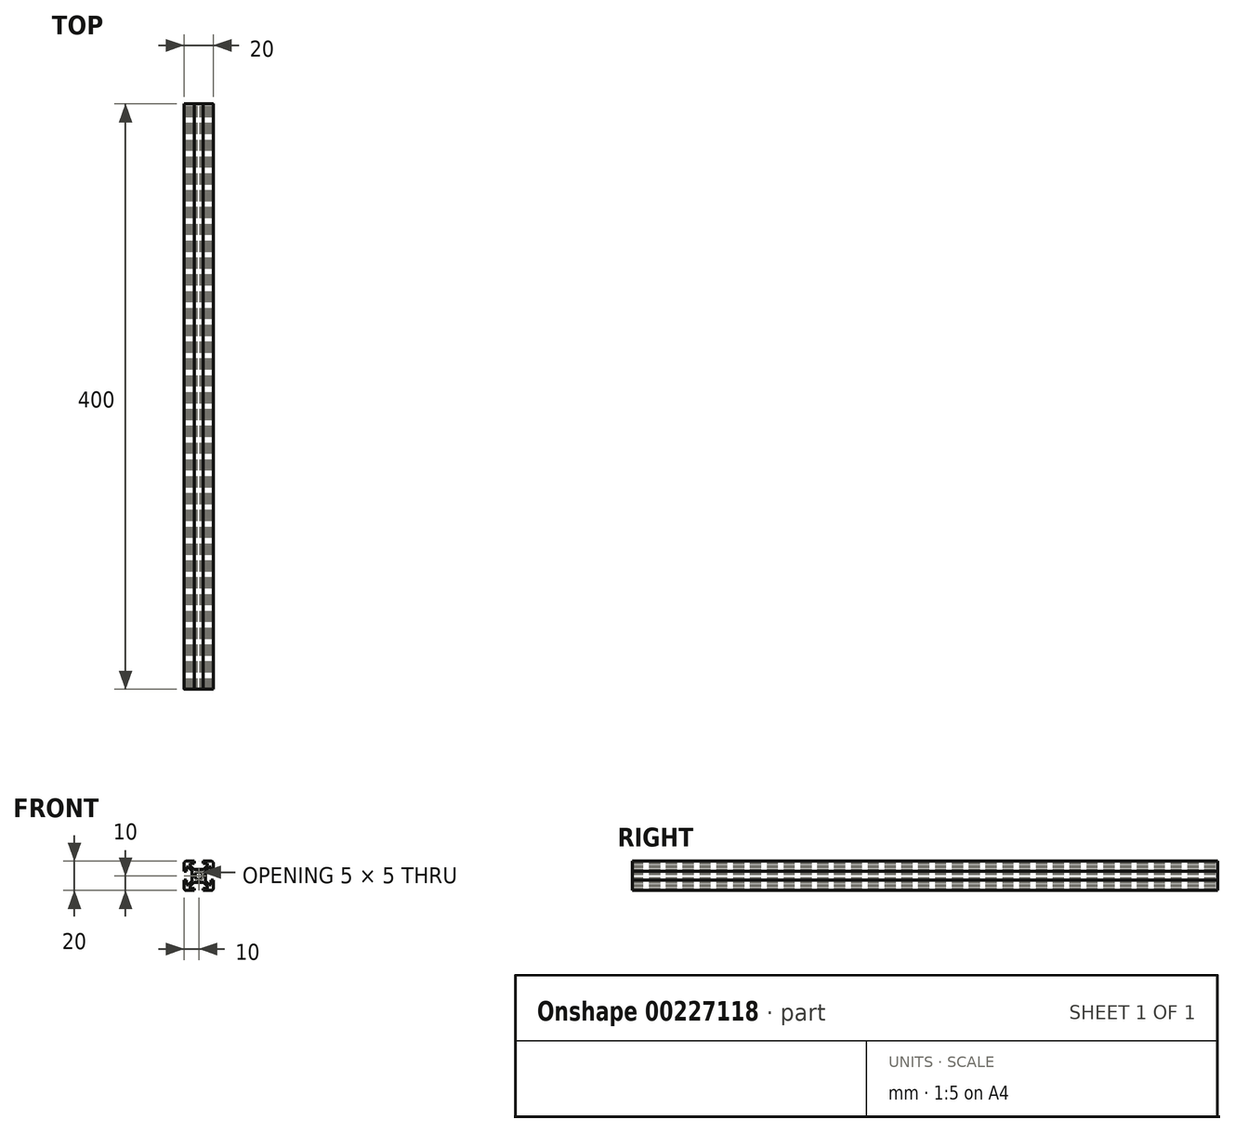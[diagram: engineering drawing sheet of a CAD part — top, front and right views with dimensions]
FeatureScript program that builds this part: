
annotation { "Feature Type Name" : "Feature", "Feature Type Description" : "" }
export const myFeature = defineFeature(function(context is Context, id is Id, definition is map)
    precondition{}
    {
        {
            var Q0;
            Q0=qCreatedBy(makeId("Front.planeOp"),FACE);
            var sketch = newSketch(context, id + "F0", { "sketchPlane" : qUnion([Q0])});
            skLineSegment(sketch, "E0.bottom", {"start": v(8.5, -10) * mm, "end": v(3, -10) * mm});
            skLineSegment(sketch, "E0.top", {"start": v(8.5, 10) * mm, "end": v(3, 10) * mm});
            skLineSegment(sketch, "E0.left", {"start": v(10, -8.5) * mm, "end": v(10, -3) * mm});
            skLineSegment(sketch, "E0.right", {"start": v(-10, -8.5) * mm, "end": v(-10, -3) * mm});
            skPoint(sketch, "E0.middle", {"position": v(0, 0) * mm});
            skLineSegment(sketch, "E1.bottom", {"start": v(6, -8.5) * mm, "end": v(3, -8.5) * mm});
            skLineSegment(sketch, "E1.top", {"start": v(6, 8.5) * mm, "end": v(3, 8.5) * mm});
            skLineSegment(sketch, "E1.left", {"start": v(8.5, -6) * mm, "end": v(8.5, -3) * mm});
            skLineSegment(sketch, "E1.right", {"start": v(-8.5, -6) * mm, "end": v(-8.5, -3) * mm});
            skLineSegment(sketch, "E2.bottom", {"start": v(3.44, -4.5) * mm, "end": v(-3.44, -4.5) * mm});
            skLineSegment(sketch, "E2.top", {"start": v(3.44, 4.5) * mm, "end": v(-3.44, 4.5) * mm});
            skLineSegment(sketch, "E2.left", {"start": v(4.5, -3.44) * mm, "end": v(4.5, 3.44) * mm});
            skLineSegment(sketch, "E2.right", {"start": v(-4.5, -3.44) * mm, "end": v(-4.5, 3.44) * mm});
            skLineSegment(sketch, "E3.bottom", {"start": v(8.5, -6) * mm, "end": v(7.06, -6) * mm});
            skLineSegment(sketch, "E3.top", {"start": v(8.5, 6) * mm, "end": v(7.06, 6) * mm});
            skLineSegment(sketch, "E4.left", {"start": v(6, -8.5) * mm, "end": v(6, -7.06) * mm});
            skLineSegment(sketch, "E4.right", {"start": v(-6, -8.5) * mm, "end": v(-6, -7.06) * mm});
            skPoint(sketch, "E5.orphan", {"position": v(-8.5, 8.5) * mm});
            skPoint(sketch, "E6.orphan", {"position": v(8.5, 8.5) * mm});
            skPoint(sketch, "E7.orphan", {"position": v(8.5, -8.5) * mm});
            skPoint(sketch, "E8.orphan", {"position": v(-8.5, -8.5) * mm});
            skLineSegment(sketch, "E9.trimOffspring", {"start": v(-6, 7.06) * mm, "end": v(-6, 8.5) * mm});
            skLineSegment(sketch, "E10.trimOffspring", {"start": v(-7.06, 6) * mm, "end": v(-8.5, 6) * mm});
            skLineSegment(sketch, "E11.trimOffspring", {"start": v(6, 7.06) * mm, "end": v(6, 8.5) * mm});
            skLineSegment(sketch, "E12.trimOffspring", {"start": v(-7.06, -6) * mm, "end": v(-8.5, -6) * mm});
            skLineSegment(sketch, "E13", {"start": v(-10, 10) * mm, "end": v(0, 0) * mm, "construction": true});
            skLineSegment(sketch, "E14", {"start": v(10, 10) * mm, "end": v(0, 0) * mm, "construction": true});
            skLineSegment(sketch, "E15", {"start": v(-6, 7.06) * mm, "end": v(-3.44, 4.5) * mm});
            skPoint(sketch, "E15.endSnap0", {"position": v(7.25, -6) * mm});
            skLineSegment(sketch, "E16", {"start": v(6, -7.06) * mm, "end": v(3.44, -4.5) * mm});
            skLineSegment(sketch, "E17", {"start": v(7.06, 6) * mm, "end": v(4.5, 3.44) * mm});
            skLineSegment(sketch, "E18", {"start": v(6, 7.06) * mm, "end": v(3.44, 4.5) * mm});
            skPoint(sketch, "E19.orphan", {"position": v(6, -6) * mm});
            skPoint(sketch, "E20.orphan", {"position": v(-4.5, -4.5) * mm});
            skPoint(sketch, "E21.orphan", {"position": v(-4.5, 4.5) * mm});
            skPoint(sketch, "E22.orphan", {"position": v(4.5, 4.5) * mm});
            skPoint(sketch, "E23.orphan", {"position": v(4.5, -4.5) * mm});
            skLineSegment(sketch, "E24.trimOffspring", {"start": v(4.5, -3.44) * mm, "end": v(7.06, -6) * mm});
            skLineSegment(sketch, "E25.trimOffspring", {"start": v(-3.44, -4.5) * mm, "end": v(-6, -7.06) * mm});
            skLineSegment(sketch, "E26.trimOffspring", {"start": v(-4.5, -3.44) * mm, "end": v(-7.06, -6) * mm});
            skLineSegment(sketch, "E27.trimOffspring", {"start": v(-4.5, 3.44) * mm, "end": v(-7.06, 6) * mm});
            skLineSegment(sketch, "E28.bottom", {"start": v(8.5, -3) * mm, "end": v(10, -3) * mm});
            skLineSegment(sketch, "E28.top", {"start": v(8.5, 3) * mm, "end": v(10, 3) * mm});
            skPoint(sketch, "E28.middle", {"position": v(10, 0) * mm});
            skLineSegment(sketch, "E29.left", {"start": v(3, 8.5) * mm, "end": v(3, 10) * mm});
            skLineSegment(sketch, "E29.right", {"start": v(-3, 8.5) * mm, "end": v(-3, 10) * mm});
            skPoint(sketch, "E29.middle", {"position": v(0, 10) * mm});
            skLineSegment(sketch, "E30.bottom", {"start": v(-8.5, 3) * mm, "end": v(-10, 3) * mm});
            skLineSegment(sketch, "E30.top", {"start": v(-8.5, -3) * mm, "end": v(-10, -3) * mm});
            skPoint(sketch, "E30.middle", {"position": v(-10, 0) * mm});
            skLineSegment(sketch, "E31.left", {"start": v(3, -8.5) * mm, "end": v(3, -10) * mm});
            skLineSegment(sketch, "E31.right", {"start": v(-3, -8.5) * mm, "end": v(-3, -10) * mm});
            skPoint(sketch, "E31.middle", {"position": v(0, -10) * mm});
            skPoint(sketch, "E32.orphan", {"position": v(3, 11.5) * mm});
            skPoint(sketch, "E33.orphan", {"position": v(-3, 11.5) * mm});
            skLineSegment(sketch, "E34.trimOffspring", {"start": v(-3, 10) * mm, "end": v(-8.5, 10) * mm});
            skLineSegment(sketch, "E35.trimOffspring", {"start": v(-3, 8.5) * mm, "end": v(-6, 8.5) * mm});
            skPoint(sketch, "E28.right.end.orphan", {"position": v(11.5, 3) * mm});
            skPoint(sketch, "E36.orphan", {"position": v(11.5, -3) * mm});
            skLineSegment(sketch, "E37.trimOffspring", {"start": v(10, 3) * mm, "end": v(10, 8.5) * mm});
            skLineSegment(sketch, "E38.trimOffspring", {"start": v(8.5, 3) * mm, "end": v(8.5, 6) * mm});
            skPoint(sketch, "E39.orphan", {"position": v(3, -11.5) * mm});
            skPoint(sketch, "E40.orphan", {"position": v(-3, -11.5) * mm});
            skLineSegment(sketch, "E41.trimOffspring", {"start": v(-3, -10) * mm, "end": v(-8.5, -10) * mm});
            skLineSegment(sketch, "E42.trimOffspring", {"start": v(-3, -8.5) * mm, "end": v(-6, -8.5) * mm});
            skPoint(sketch, "E30.right.end.orphan", {"position": v(-11.5, -3) * mm});
            skPoint(sketch, "E43.orphan", {"position": v(-11.5, 3) * mm});
            skLineSegment(sketch, "E44.trimOffspring", {"start": v(-10, 3) * mm, "end": v(-10, 8.5) * mm});
            skLineSegment(sketch, "E45.trimOffspring", {"start": v(-8.5, 3) * mm, "end": v(-8.5, 6) * mm});
            skLineSegment(sketch, "E46.trimOffspring", {"start": v(0, 0) * mm, "end": v(10, -10) * mm, "construction": true});
            skLineSegment(sketch, "E47.trimOffspring", {"start": v(0, 0) * mm, "end": v(-10, -10) * mm, "construction": true});
            skArc(sketch, "E48", {"start": v(1.16, 2.22) * mm, "mid": v(0, 2.5) * mm, "end": v(-1.16, 2.22) * mm});
            skLineSegment(sketch, "E49", {"start": v(-2.5, -1.44) * mm, "end": v(1.44, 2.5) * mm});
            skLineSegment(sketch, "E50", {"start": v(2.5, 1.44) * mm, "end": v(-1.44, -2.5) * mm});
            skLineSegment(sketch, "E51", {"start": v(1.44, -2.5) * mm, "end": v(-2.5, 1.44) * mm});
            skLineSegment(sketch, "E52", {"start": v(-1.44, 2.5) * mm, "end": v(2.5, -1.44) * mm});
            skLineSegment(sketch, "E53", {"start": v(2.5, 1.44) * mm, "end": v(2.5, -1.44) * mm, "construction": true});
            skLineSegment(sketch, "E54", {"start": v(1.44, -2.5) * mm, "end": v(-1.44, -2.5) * mm, "construction": true});
            skLineSegment(sketch, "E55", {"start": v(-2.5, -1.44) * mm, "end": v(-2.5, 1.44) * mm, "construction": true});
            skLineSegment(sketch, "E56", {"start": v(-1.44, 2.5) * mm, "end": v(1.44, 2.5) * mm, "construction": true});
            skLineSegment(sketch, "E57", {"start": v(-1.44, 2.5) * mm, "end": v(-2.5, 1.44) * mm});
            skLineSegment(sketch, "E58", {"start": v(1.44, 2.5) * mm, "end": v(2.5, 1.44) * mm});
            skLineSegment(sketch, "E59", {"start": v(2.5, -1.44) * mm, "end": v(1.44, -2.5) * mm});
            skLineSegment(sketch, "E60", {"start": v(-1.44, -2.5) * mm, "end": v(-2.5, -1.44) * mm});
            skArc(sketch, "E61.trimOffspring", {"start": v(-2.22, 1.16) * mm, "mid": v(-2.5, 0) * mm, "end": v(-2.22, -1.16) * mm});
            skArc(sketch, "E62.trimOffspring", {"start": v(-1.16, -2.22) * mm, "mid": v(0, -2.5) * mm, "end": v(1.16, -2.22) * mm});
            skArc(sketch, "E63.trimOffspring", {"start": v(2.22, -1.16) * mm, "mid": v(2.5, 0) * mm, "end": v(2.22, 1.16) * mm});
            skPoint(sketch, "E64.visualSharp", {"position": v(10, 10) * mm});
            skArc(sketch, "E64.filletArc", {"start": v(10, 8.5) * mm, "mid": v(9.56, 9.56) * mm, "end": v(8.5, 10) * mm});
            skPoint(sketch, "E65.visualSharp", {"position": v(10, -10) * mm});
            skArc(sketch, "E65.filletArc", {"start": v(8.5, -10) * mm, "mid": v(9.56, -9.56) * mm, "end": v(10, -8.5) * mm});
            skPoint(sketch, "E66.visualSharp", {"position": v(-10, -10) * mm});
            skArc(sketch, "E66.filletArc", {"start": v(-10, -8.5) * mm, "mid": v(-9.56, -9.56) * mm, "end": v(-8.5, -10) * mm});
            skPoint(sketch, "E67.visualSharp", {"position": v(-10, 10) * mm});
            skArc(sketch, "E67.filletArc", {"start": v(-8.5, 10) * mm, "mid": v(-9.56, 9.56) * mm, "end": v(-10, 8.5) * mm});
            skSolve(sketch);
        }
        {
            assignVariable(context, id + "F2", {"name" : "Length", "anyValue" : 400});
        }
        {
            var Q0;
            Q0=qSketchRegion(id+"F0",true);
            extrude(context, id + "F1", {"entities" : qUnion([Q0]), "depth" : (getVariable(context, 'Length')) * mm});
        }
    });
